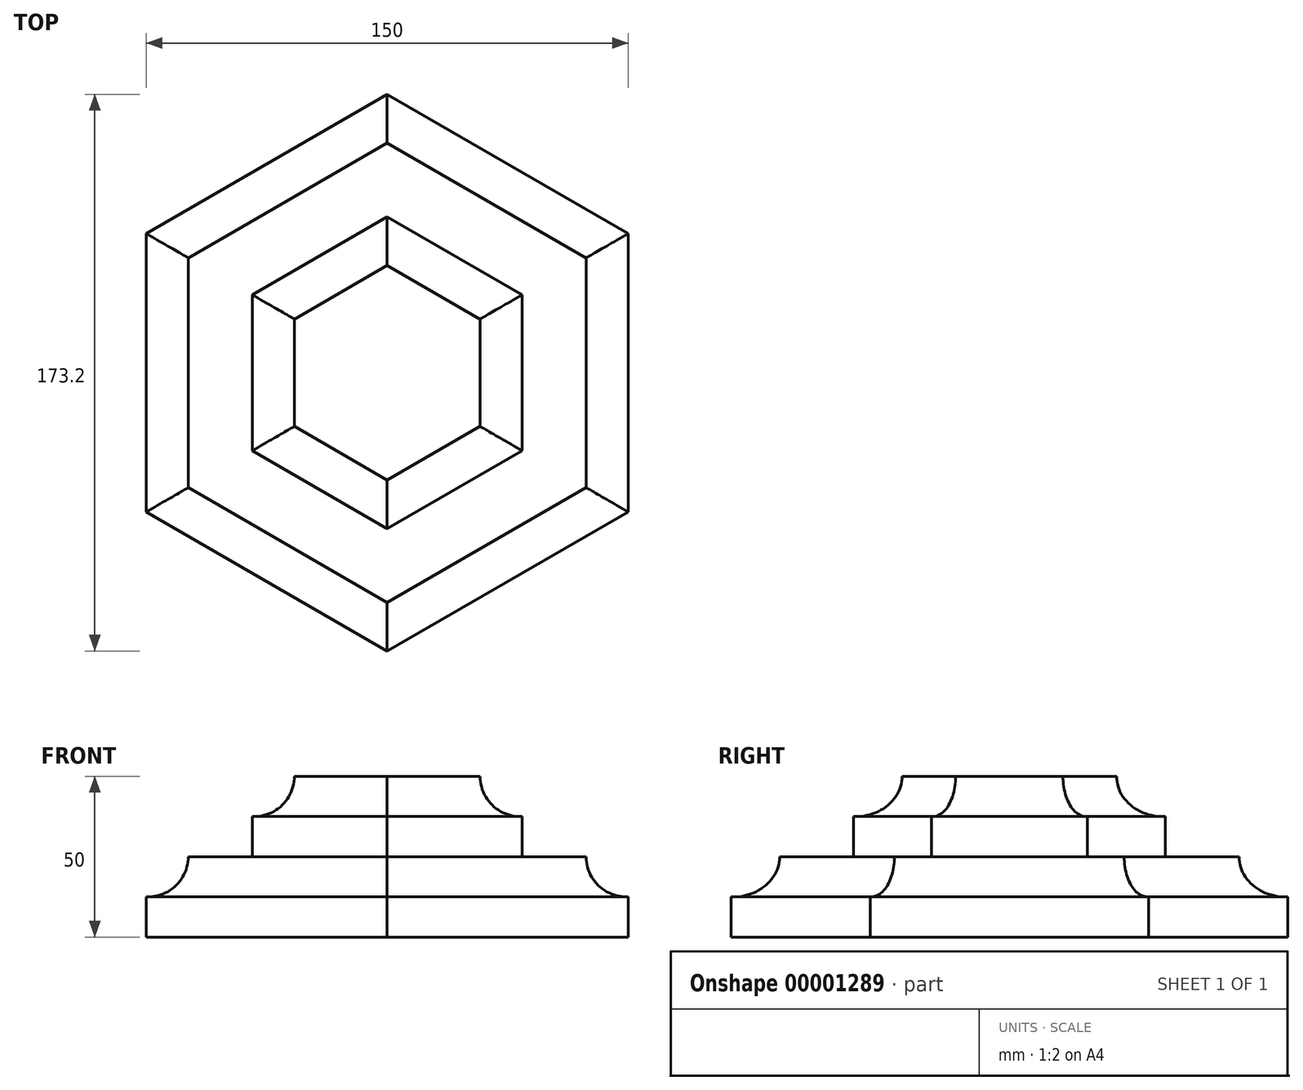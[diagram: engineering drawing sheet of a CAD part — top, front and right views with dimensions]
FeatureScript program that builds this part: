
annotation { "Feature Type Name" : "Feature", "Feature Type Description" : "" }
export const myFeature = defineFeature(function(context is Context, id is Id, definition is map)
    precondition{}
    {
        {
            var Q0;
            Q0=qCreatedBy(makeId("Top.planeOp"),FACE);
            var sketch = newSketch(context, id + "F0", { "sketchPlane" : qUnion([Q0])});
            skCircle(sketch, "E0.cCircle", {"center": v(0, 0) * mm, "radius": 75 * mm, "construction": true});
            skLineSegment(sketch, "E0.0", {"start": v(75, 43.3) * mm, "end": v(75, -43.3) * mm});
            skLineSegment(sketch, "E0.1", {"start": v(75, -43.3) * mm, "end": v(0, -86.6) * mm});
            skLineSegment(sketch, "E0.2", {"start": v(0, -86.6) * mm, "end": v(-75, -43.3) * mm});
            skLineSegment(sketch, "E0.3", {"start": v(-75, -43.3) * mm, "end": v(-75, 43.3) * mm});
            skLineSegment(sketch, "E0.4", {"start": v(-75, 43.3) * mm, "end": v(0, 86.6) * mm});
            skLineSegment(sketch, "E0.5", {"start": v(0, 86.6) * mm, "end": v(75, 43.3) * mm});
            skPoint(sketch, "E0.0.midPoint", {"position": v(75, 0) * mm});
            skCircle(sketch, "E1.cCircle", {"center": v(0, 0) * mm, "radius": 48.5 * mm, "construction": true});
            skLineSegment(sketch, "E1.0", {"start": v(0, 48.5) * mm, "end": v(42, 24.25) * mm});
            skLineSegment(sketch, "E1.1", {"start": v(42, 24.25) * mm, "end": v(42, -24.25) * mm});
            skLineSegment(sketch, "E1.2", {"start": v(42, -24.25) * mm, "end": v(0, -48.5) * mm});
            skLineSegment(sketch, "E1.3", {"start": v(0, -48.5) * mm, "end": v(-42, -24.25) * mm});
            skLineSegment(sketch, "E1.4", {"start": v(-42, -24.25) * mm, "end": v(-42, 24.25) * mm});
            skLineSegment(sketch, "E1.5", {"start": v(-42, 24.25) * mm, "end": v(0, 48.5) * mm});
            skSolve(sketch);
        }
        {
            var Q0;
            Q0=makeQuery(id+"F0.imprint","IMPRINT",FACE,{"disambiguationData":[TD([[makeQuery(id+"F0.imprint","IMPRINT",EDGE,{"derivedFrom":sQuery(id+"F0.wireOp",EDGE,"E0.0")}),-1.0]])]});
            var Q1;
            Q1=makeQuery(id+"F0.imprint","IMPRINT",FACE,{"disambiguationData":[TD([[makeQuery(id+"F0.imprint","IMPRINT",EDGE,{"derivedFrom":sQuery(id+"F0.wireOp",EDGE,"E1.0")}),-1.0]])]});
            extrude(context, id + "F1", {"entities" : qUnion([Q0, Q1]), "depth" : 25 * mm});
        }
        {
            var Q0;
            Q0=qCreatedBy(makeId("Front.planeOp"),FACE);
            var sketch = newSketch(context, id + "F2", { "sketchPlane" : qUnion([Q0])});
            skCircle(sketch, "E2", {"center": v(74.4, 25) * mm, "radius": 12.5 * mm});
            skLineSegment(sketch, "E3", {"start": v(74.4, 25) * mm, "end": v(41.4, 25) * mm});
            skLineSegment(sketch, "E4", {"start": v(41.4, 25) * mm, "end": v(41.4, 50) * mm});
            skCircle(sketch, "E5", {"center": v(41.4, 50) * mm, "radius": 12.5 * mm});
            skSolve(sketch);
        }
        {
            var Q0;
            Q0=makeQuery(id+"F2.imprint","IMPRINT",FACE,{"disambiguationData":[TD([[makeQuery(id+"F2.imprint","IMPRINT",EDGE,{"derivedFrom":sQuery(id+"F2.wireOp",EDGE,"E2")}),1.0]])]});
            var Q1;
            Q1=makeQuery(id+"F1.opExtrude","CAP_EDGE",EDGE,{"disambiguationData":[OSD([sQuery(id+"F0.wireOp",EDGE,"E0.0")])],"isStart":false});
            var Q2;
            Q2=makeQuery(id+"F1.opExtrude","CAP_EDGE",EDGE,{"disambiguationData":[OSD([sQuery(id+"F0.wireOp",EDGE,"E0.1")])],"isStart":false});
            var Q3;
            Q3=makeQuery(id+"F1.opExtrude","CAP_EDGE",EDGE,{"disambiguationData":[OSD([sQuery(id+"F0.wireOp",EDGE,"E0.2")])],"isStart":false});
            var Q4;
            Q4=makeQuery(id+"F1.opExtrude","CAP_EDGE",EDGE,{"disambiguationData":[OSD([sQuery(id+"F0.wireOp",EDGE,"E0.3")])],"isStart":false});
            var Q5;
            Q5=makeQuery(id+"F1.opExtrude","CAP_EDGE",EDGE,{"disambiguationData":[OSD([sQuery(id+"F0.wireOp",EDGE,"E0.4")])],"isStart":false});
            var Q6;
            Q6=makeQuery(id+"F1.opExtrude","CAP_EDGE",EDGE,{"disambiguationData":[OSD([sQuery(id+"F0.wireOp",EDGE,"E0.5")])],"isStart":false});
            sweep(context, id + "F3", {"operationType" : NewBodyOperationType.REMOVE, "profiles" : qUnion([Q0]), "path" : qUnion([Q1, Q2, Q3, Q4, Q5, Q6])});
        }
        {
            var Q0;
            Q0=makeQuery(id+"F1.opExtrude","CAP_FACE",FACE,{"disambiguationData":[OSD([sQuery(id+"F0.wireOp",EDGE,"E0.0"),sQuery(id+"F0.wireOp",EDGE,"E0.1"),sQuery(id+"F0.wireOp",EDGE,"E0.2"),sQuery(id+"F0.wireOp",EDGE,"E0.3"),sQuery(id+"F0.wireOp",EDGE,"E0.4"),sQuery(id+"F0.wireOp",EDGE,"E0.5")])],"isStart":false});
            var sketch = newSketch(context, id + "F4", { "sketchPlane" : qUnion([Q0])});
            skLineSegment(sketch, "E6.0", {"start": v(42, 24.25) * mm, "end": v(42, -24.25) * mm});
            skLineSegment(sketch, "E7.0", {"start": v(42, -24.25) * mm, "end": v(0, -48.5) * mm});
            skLineSegment(sketch, "E8.0", {"start": v(0, -48.5) * mm, "end": v(-42, -24.25) * mm});
            skLineSegment(sketch, "E9.0", {"start": v(-42, -24.25) * mm, "end": v(-42, 24.25) * mm});
            skLineSegment(sketch, "E10.0", {"start": v(-42, 24.25) * mm, "end": v(0, 48.5) * mm});
            skLineSegment(sketch, "E11.0", {"start": v(0, 48.5) * mm, "end": v(42, 24.25) * mm});
            skSolve(sketch);
        }
        {
            var Q0;
            Q0=makeQuery(id+"F4.imprint","IMPRINT",FACE,{"disambiguationData":[TD([[makeQuery(id+"F4.imprint","IMPRINT",EDGE,{"derivedFrom":sQuery(id+"F4.wireOp",EDGE,"E6.0")}),-1.0]])]});
            extrude(context, id + "F5", {"entities" : qUnion([Q0]), "operationType" : NewBodyOperationType.ADD, "depth" : 25 * mm});
        }
        {
            var Q0;
            Q0=makeQuery(id+"F2.imprint","IMPRINT",FACE,{"disambiguationData":[TD([[makeQuery(id+"F2.imprint","IMPRINT",EDGE,{"derivedFrom":sQuery(id+"F2.wireOp",EDGE,"E5")}),1.0]])]});
            var Q1;
            Q1=makeQuery(id+"F5.opExtrude","CAP_EDGE",EDGE,{"disambiguationData":[OSD([sQuery(id+"F4.wireOp",EDGE,"E6.0")])],"isStart":false});
            var Q2;
            Q2=makeQuery(id+"F5.opExtrude","CAP_EDGE",EDGE,{"disambiguationData":[OSD([sQuery(id+"F4.wireOp",EDGE,"E7.0")])],"isStart":false});
            var Q3;
            Q3=makeQuery(id+"F5.opExtrude","CAP_EDGE",EDGE,{"disambiguationData":[OSD([sQuery(id+"F4.wireOp",EDGE,"E8.0")])],"isStart":false});
            var Q4;
            Q4=makeQuery(id+"F5.opExtrude","CAP_EDGE",EDGE,{"disambiguationData":[OSD([sQuery(id+"F4.wireOp",EDGE,"E9.0")])],"isStart":false});
            var Q5;
            Q5=makeQuery(id+"F5.opExtrude","CAP_EDGE",EDGE,{"disambiguationData":[OSD([sQuery(id+"F4.wireOp",EDGE,"E10.0")])],"isStart":false});
            var Q6;
            Q6=makeQuery(id+"F5.opExtrude","CAP_EDGE",EDGE,{"disambiguationData":[OSD([sQuery(id+"F4.wireOp",EDGE,"E11.0")])],"isStart":false});
            sweep(context, id + "F6", {"operationType" : NewBodyOperationType.REMOVE, "profiles" : qUnion([Q0]), "path" : qUnion([Q1, Q2, Q3, Q4, Q5, Q6])});
        }
    });
